# Revit family: Фильтр карманный укороченный LITENED FRU
name_source: partatom
category: Оборудование
revit_build: Autodesk Revit 2017 (Build: 20160225_1515(x64)
units: mm (PartAtom-declared; Revit-internal decimal feet)

## family parameters
Всегда вертикально = Да
На основе рабочей плоскости = Нет
Общий = Нет
При загрузке вырезать с полостями = Нет
Размер круглого соединителя = Использовать диаметр
Тип детали = Нормальный
Точка расчета площади = Нет

## types (8) — shared parameters
h = 60 мм
Д = 350 мм
Д1 = 330 мм
Единица измерения = шт.
Завод изготовитель = NED
Ключевая пометка = Вентиляция
Наименование и тех.хар-ка = Фильтр карманный укороченный
Раздел = ОВ
УГО 100-50 = Нет
УГО 90-50 = Нет
высота ножек = 50 мм

## per-type parameters (varying)
| type | А | А1 | Б | Б1 | Г | Диаметр патрубков | Масса единицы | Материал | Середина | Тип, марка, обозначение | УГО 50-25 | УГО 60-30 | УГО 60-35 | УГО 70-40 | УГО 80-50 | высота | размер В | ширина |
| 50-25 | 710 мм | 690 мм | 470 мм | 450 мм | 400 мм | 20 мм | 16.5 | Сталь серая | 240 мм | LITENED 50-25 FRU | Да | Нет | Нет | Нет | Нет | 250 мм | 640 мм | 500 мм |
| 50-30 | 710 мм | 690 мм | 520 мм | 500 мм | 450 мм | 20 мм | 17 | Сталь серая | 260 мм | LITENED 50-30 FRU | Да | Нет | Нет | Нет | Нет | 300 мм | 640 мм | 500 мм |
| 60-30 | 810 мм | 790 мм | 520 мм | 500 мм | 450 мм | 20 мм | 19 | Сталь серая | 260 мм | LITENED 60-30 FRU | Нет | Да | Нет | Нет | Нет | 300 мм | 740 мм | 600 мм |
| 60-35 | 810 мм | 790 мм | 570 мм | 550 мм | 500 мм | 20 мм | 20 | Сталь серая | 290 мм | LITENED 60-35 FRU | Нет | Нет | Да | Нет | Нет | 350 мм | 740 мм | 600 мм |
| 70-40 | 910 мм | 890 мм | 620 мм | 600 мм | 550 мм | 30 мм | 22 | Сталь серая | 310 мм | LITENED 70-40 FRU | Нет | Нет | Нет | Да | Нет | 400 мм | 840 мм | 700 мм |
| 80-50 | 1010 мм | 990 мм | 720 мм | 700 мм | 650 мм | 30 мм | 24 | RAL 0000 Серый металл | 360 мм | LITENED 80-50 FRU | Нет | Нет | Нет | Нет | Да | 500 мм | 940 мм | 800 мм |
| 90-50 | 1130 мм | 1110 мм | 740 мм | 720 мм | 650 мм | 40 мм | 26 | Сталь серая | 370 мм | LITENED 90-50 FRU | Нет | Нет | Нет | Нет | Да | 500 мм | 1050 мм | 900 мм |
| 100-50 | 1230 мм | 1210 мм | 740 мм | 720 мм | 670 мм | 40 мм | 28 | Сталь серая | 370 мм | LITENED 100-50 FRU | Нет | Нет | Нет | Нет | Да | 500 мм | 1150 мм | 1000 мм |
